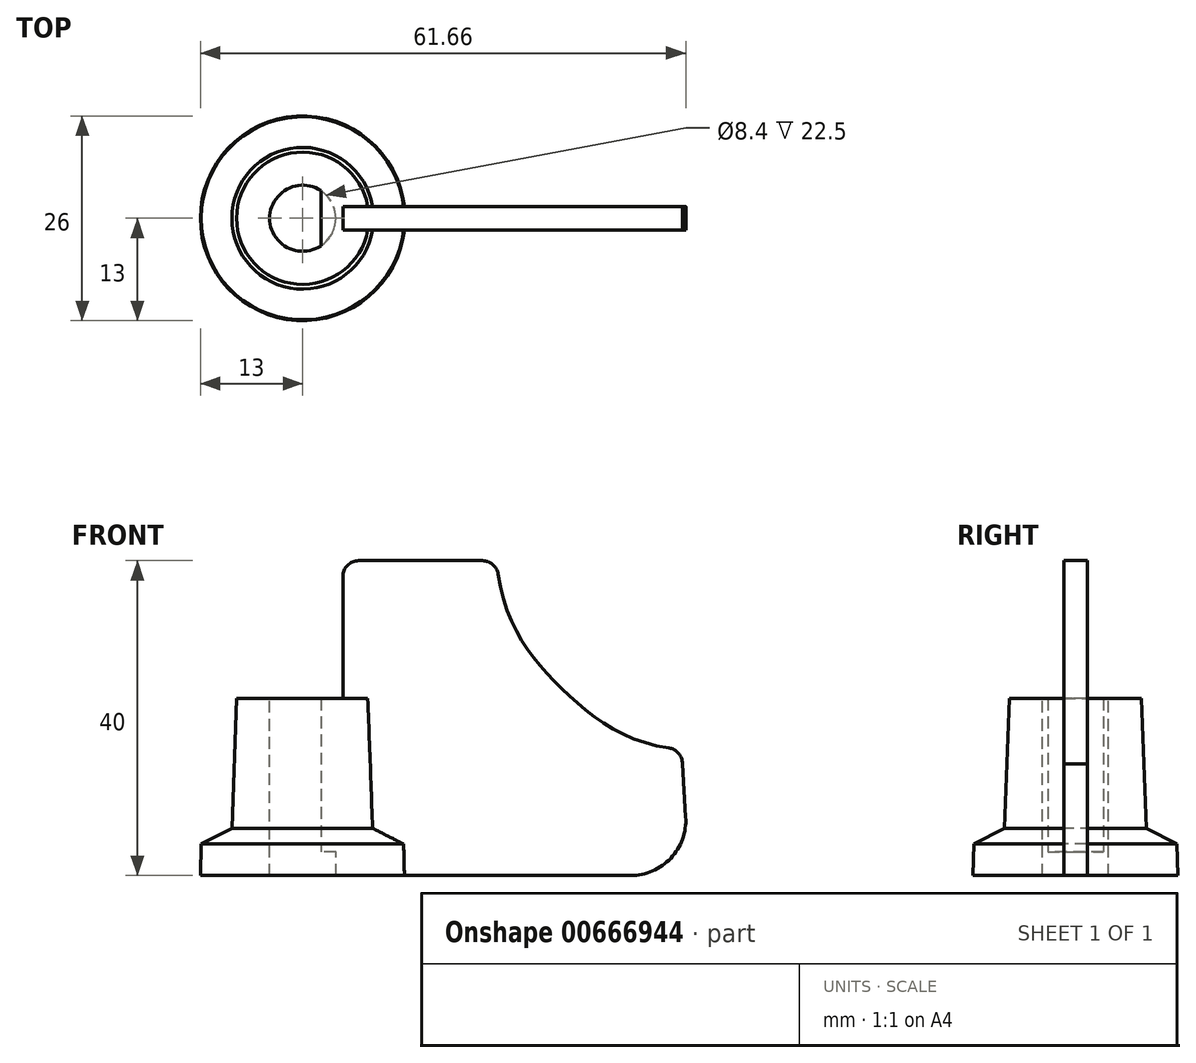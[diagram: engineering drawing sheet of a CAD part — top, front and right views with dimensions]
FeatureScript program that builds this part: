
annotation { "Feature Type Name" : "Feature", "Feature Type Description" : "" }
export const myFeature = defineFeature(function(context is Context, id is Id, definition is map)
    precondition{}
    {
        {
            var Q0;
            Q0=qCreatedBy(makeId("Front.planeOp"),FACE);
            var sketch = newSketch(context, id + "F0", { "sketchPlane" : qUnion([Q0])});
            skLineSegment(sketch, "E0", {"start": v(4.2, 0) * mm, "end": v(4.2, 22.5) * mm});
            skLineSegment(sketch, "E1", {"start": v(4.2, 22.5) * mm, "end": v(8.4, 22.5) * mm});
            skLineSegment(sketch, "E2", {"start": v(8.4, 22.5) * mm, "end": v(9, 6) * mm});
            skLineSegment(sketch, "E3", {"start": v(9, 6) * mm, "end": v(12.9, 4) * mm});
            skLineSegment(sketch, "E4", {"start": v(12.9, 4) * mm, "end": v(13, 0) * mm});
            skLineSegment(sketch, "E5", {"start": v(13, 0) * mm, "end": v(4.2, 0) * mm});
            skLineSegment(sketch, "E6", {"start": v(0, 31.2) * mm, "end": v(0, -9.04) * mm, "construction": true});
            skSolve(sketch);
        }
        {
            var Q0;
            Q0=makeQuery(id+"F0.imprint","IMPRINT",FACE,{"disambiguationData":[TD([[makeQuery(id+"F0.imprint","IMPRINT",EDGE,{"derivedFrom":sQuery(id+"F0.wireOp",EDGE,"E0")}),-1.0]])]});
            var Q1;
            Q1=sQuery(id+"F0.wireOp",EDGE,"E6");
            revolve(context, id + "F1", {"entities" : qUnion([Q0]), "axis" : qUnion([Q1]), "revolveType" : RevolveType.FULL});
        }
        {
            var Q0;
            Q0=qCreatedBy(makeId("Front.planeOp"),FACE);
            var sketch = newSketch(context, id + "F2", { "sketchPlane" : qUnion([Q0])});
            skLineSegment(sketch, "E7", {"start": v(22.83, 40) * mm, "end": v(7.1, 40) * mm});
            skLineSegment(sketch, "E8", {"start": v(5.1, 38) * mm, "end": v(5.1, 0) * mm});
            skFitSpline(sketch, "E9", {"points": [v(24.6, 40) * mm, v(32.59, 24.04) * mm, v(49.1, 16) * mm], "startDerivative": vector(4.54, -46.81) * mm, "endDerivative": vector(44.73, -0.89) * mm});
            skArc(sketch, "E10.filletArc", {"start": v(24.81, 38.3) * mm, "mid": v(24.14, 39.52) * mm, "end": v(22.83, 40) * mm});
            skPoint(sketch, "E11.visualSharp", {"position": v(5.1, 40) * mm});
            skArc(sketch, "E11.filletArc", {"start": v(7.1, 40) * mm, "mid": v(5.69, 39.41) * mm, "end": v(5.1, 38) * mm});
            skArc(sketch, "E12.filletArc", {"start": v(48.23, 14.2) * mm, "mid": v(47.74, 15.53) * mm, "end": v(46.5, 16.2) * mm});
            skPoint(sketch, "E13.visualSharp", {"position": v(49.1, 0) * mm});
            skLineSegment(sketch, "E14", {"start": v(5.1, 0) * mm, "end": v(41.66, 0) * mm});
            skLineSegment(sketch, "E15", {"start": v(48.23, 14.2) * mm, "end": v(48.64, 7.43) * mm});
            skArc(sketch, "E16.filletArc", {"start": v(41.66, 0) * mm, "mid": v(46.76, 2.2) * mm, "end": v(48.64, 7.43) * mm});
            skSolve(sketch);
        }
        {
            var Q0;
            Q0=makeQuery(id+"F2.imprint","IMPRINT",FACE,{"disambiguationData":[TD([[makeQuery(id+"F2.imprint","IMPRINT",EDGE,{"derivedFrom":sQuery(id+"F2.wireOp",EDGE,"E7")}),1.0]])]});
            extrude(context, id + "F3", {"entities" : qUnion([Q0]), "operationType" : NewBodyOperationType.ADD, "endBound" : BoundingType.SYMMETRIC, "depth" : 3 * mm, "offsetDistance" : 25 * mm});
        }
        {
            var Q0;
            Q0=qCreatedBy(makeId("Top.planeOp"),FACE);
            cPlane(context, id + "F4", {"entities" : qUnion([Q0]), "cplaneType" : CPlaneType.OFFSET, "offset" : 3 * mm, "width" : 150 * mm, "height" : 150 * mm});
        }
        {
            var Q0;
            Q0=qCreatedBy(id+"F4.planeOp",FACE);
            var sketch = newSketch(context, id + "F5", { "sketchPlane" : qUnion([Q0])});
            skArc(sketch, "E17", {"start": v(2.3, -3.51) * mm, "mid": v(4.2, 0) * mm, "end": v(2.3, 3.51) * mm});
            skLineSegment(sketch, "E18", {"start": v(2.3, 3.51) * mm, "end": v(2.3, -3.51) * mm});
            skSolve(sketch);
        }
        {
            var Q0;
            Q0=makeQuery(id+"F5.imprint","IMPRINT",FACE,{"disambiguationData":[TD([[makeQuery(id+"F5.imprint","IMPRINT",EDGE,{"derivedFrom":sQuery(id+"F5.wireOp",EDGE,"E17")}),1.0]])]});
            extrude(context, id + "F6", {"entities" : qUnion([Q0]), "operationType" : NewBodyOperationType.ADD, "depth" : 19.5 * mm, "offsetDistance" : 25 * mm});
        }
    });
